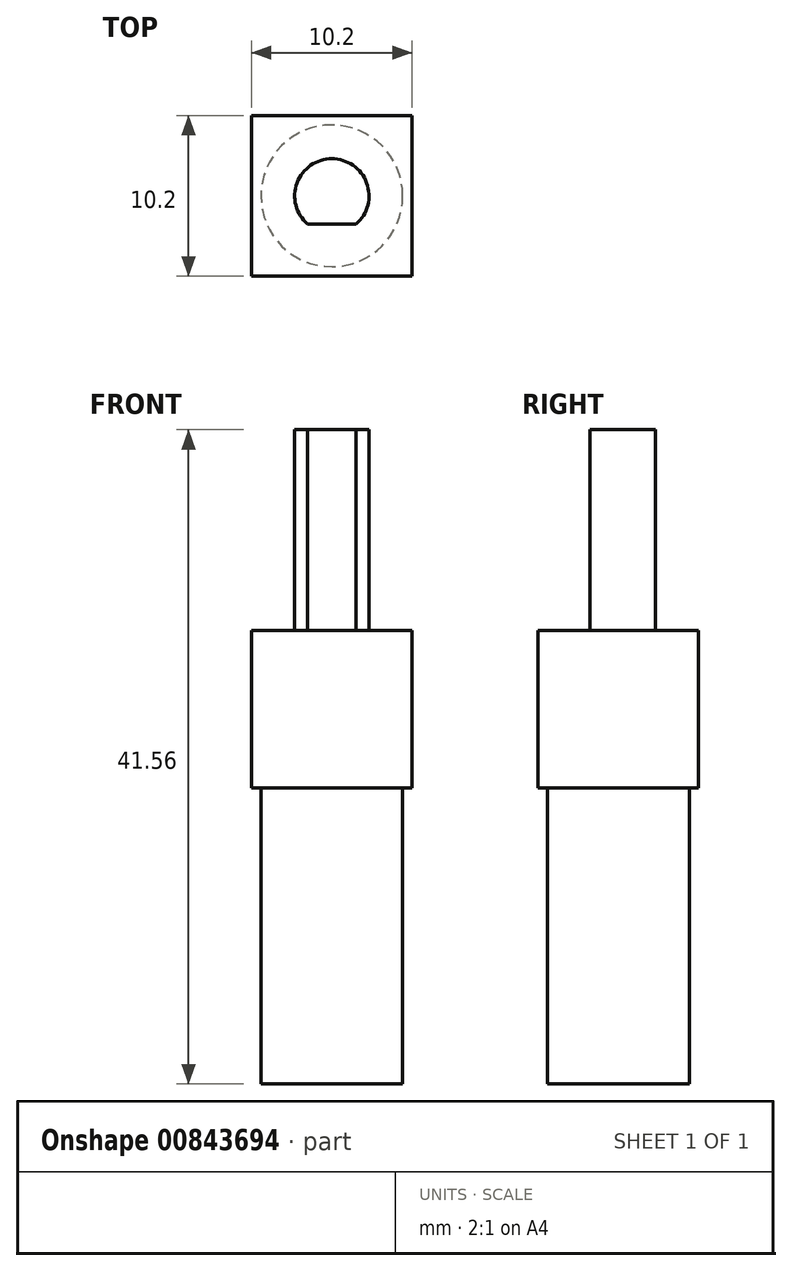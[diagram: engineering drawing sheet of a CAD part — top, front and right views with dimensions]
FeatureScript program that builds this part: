
annotation { "Feature Type Name" : "Feature", "Feature Type Description" : "" }
export const myFeature = defineFeature(function(context is Context, id is Id, definition is map)
    precondition{}
    {
        {
            var Q0;
            Q0=qCreatedBy(makeId("Top.planeOp"),FACE);
            var sketch = newSketch(context, id + "F0", { "sketchPlane" : qUnion([Q0])});
            skCircle(sketch, "E0", {"center": v(0, 0) * mm, "radius": 4.5 * mm});
            skSolve(sketch);
        }
        {
            var Q0;
            Q0=qSketchRegion(id+"F0",true);
            extrude(context, id + "F1", {"entities" : qUnion([Q0]), "depth" : 18.8 * mm, "offsetDistance" : 25.4 * mm});
        }
        {
            var Q0;
            Q0=makeQuery(id+"F1.opExtrude","CAP_FACE",FACE,{"disambiguationData":[OSD([sQuery(id+"F0.wireOp",EDGE,"E0")])],"isStart":false});
            var sketch = newSketch(context, id + "F2", { "sketchPlane" : qUnion([Q0])});
            skPoint(sketch, "E1.middle", {"position": v(0, 0) * mm});
            skLineSegment(sketch, "E2.bottom", {"start": v(-5.1, 5.1) * mm, "end": v(5.1, 5.1) * mm});
            skLineSegment(sketch, "E2.top", {"start": v(-5.1, -5.1) * mm, "end": v(5.1, -5.1) * mm});
            skLineSegment(sketch, "E2.left", {"start": v(-5.1, 5.1) * mm, "end": v(-5.1, -5.1) * mm});
            skLineSegment(sketch, "E2.right", {"start": v(5.1, 5.1) * mm, "end": v(5.1, -5.1) * mm});
            skSolve(sketch);
        }
        {
            var Q0;
            Q0=qSketchRegion(id+"F2",true);
            extrude(context, id + "F3", {"entities" : qUnion([Q0]), "operationType" : NewBodyOperationType.ADD, "depth" : 10 * mm, "offsetDistance" : 25.4 * mm});
        }
        {
            var Q0;
            Q0=makeQuery(id+"F3.opExtrude","CAP_FACE",FACE,{"disambiguationData":[OSD([sQuery(id+"F2.wireOp",EDGE,"E2.bottom"),sQuery(id+"F2.wireOp",EDGE,"E2.top"),sQuery(id+"F2.wireOp",EDGE,"E2.left"),sQuery(id+"F2.wireOp",EDGE,"E2.right")])],"isStart":false});
            var sketch = newSketch(context, id + "F4", { "sketchPlane" : qUnion([Q0])});
            skCircle(sketch, "E3", {"center": v(0, 0) * mm, "radius": 2.36 * mm});
            skSolve(sketch);
        }
        {
            var Q0;
            Q0 = qSketchRegion(id + "F4", true);
            extrude(context, id + "F5", {"entities" : qUnion([Q0]), "operationType" : NewBodyOperationType.ADD, "depth" : 12.75 * mm, "offsetDistance" : 25 * mm});
        }
        {
            var Q0;
            Q0=makeQuery(id+"F5.opExtrude","CAP_FACE",FACE,{"disambiguationData":[OSD([sQuery(id+"F4.wireOp",EDGE,"E3")])],"isStart":false});
            var sketch = newSketch(context, id + "F6", { "sketchPlane" : qUnion([Q0])});
            skLineSegment(sketch, "E4", {"start": v(0, -2.36) * mm, "end": v(0, -1.79) * mm});
            skLineSegment(sketch, "E5", {"start": v(0, -1.79) * mm, "end": v(1.54, -1.79) * mm});
            skLineSegment(sketch, "E6", {"start": v(1.54, -1.79) * mm, "end": v(-1.54, -1.79) * mm});
            skArc(sketch, "E7", {"start": v(1.54, -1.8) * mm, "mid": v(0, -2.36) * mm, "end": v(-1.54, -1.79) * mm});
            skSolve(sketch);
        }
        {
            var Q0;
            Q0 = qSketchRegion(id + "F6", true);
            extrude(context, id + "F7", {"entities" : qUnion([Q0]), "operationType" : NewBodyOperationType.REMOVE, "oppositeDirection" : true, "depth" : 12.75 * mm, "offsetDistance" : 25 * mm});
        }
    });
